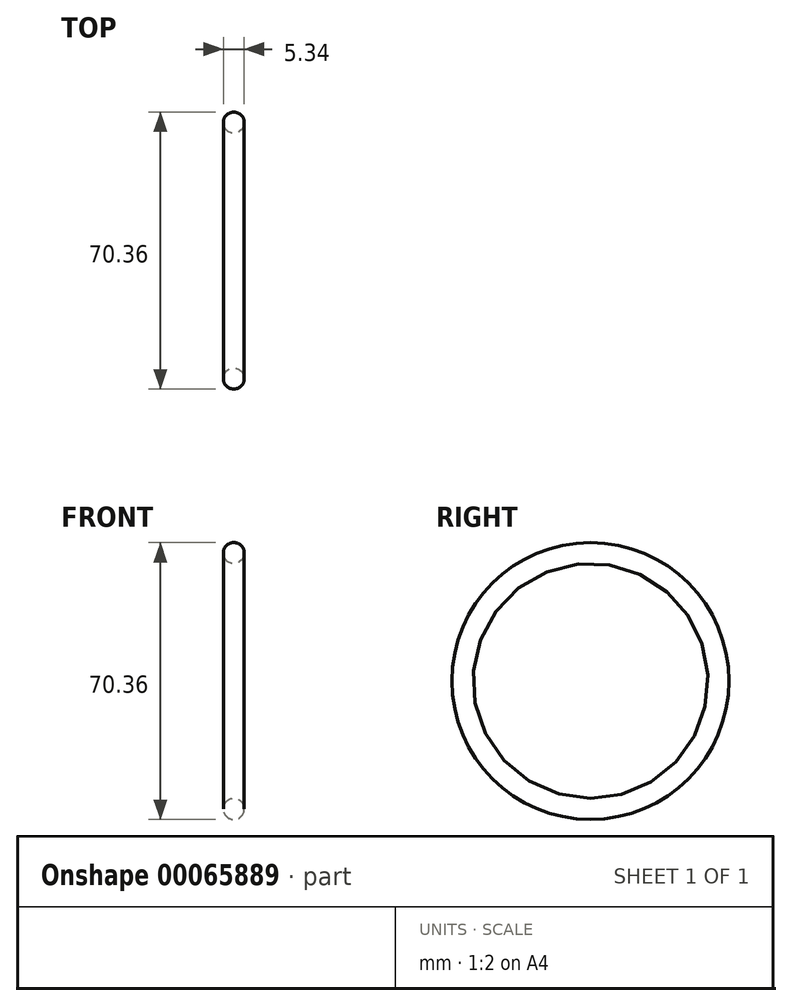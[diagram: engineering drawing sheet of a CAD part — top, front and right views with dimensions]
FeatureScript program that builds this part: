
annotation { "Feature Type Name" : "Feature", "Feature Type Description" : "" }
export const myFeature = defineFeature(function(context is Context, id is Id, definition is map)
    precondition{}
    {
        {
            var Q0;
            Q0=qCreatedBy(makeId("Front.planeOp"),FACE);
            var sketch = newSketch(context, id + "F0", { "sketchPlane" : qUnion([Q0])});
            skLineSegment(sketch, "E0", {"start": v(0, 0) * mm, "end": v(-6.06, 0) * mm, "construction": true});
            skCircle(sketch, "E1", {"center": v(0, 32.51) * mm, "radius": 2.67 * mm});
            skSolve(sketch);
        }
        {
            var Q0;
            Q0=makeQuery(id+"F0.imprint","IMPRINT",FACE,{"disambiguationData":[TD([[makeQuery(id+"F0.imprint","IMPRINT",EDGE,{"derivedFrom":sQuery(id+"F0.wireOp",EDGE,"E1")}),1.0]])]});
            var Q1;
            Q1=sQuery(id+"F0.wireOp",EDGE,"E0");
            revolve(context, id + "F1", {"entities" : qUnion([Q0]), "axis" : qUnion([Q1]), "revolveType" : RevolveType.FULL});
        }
    });
